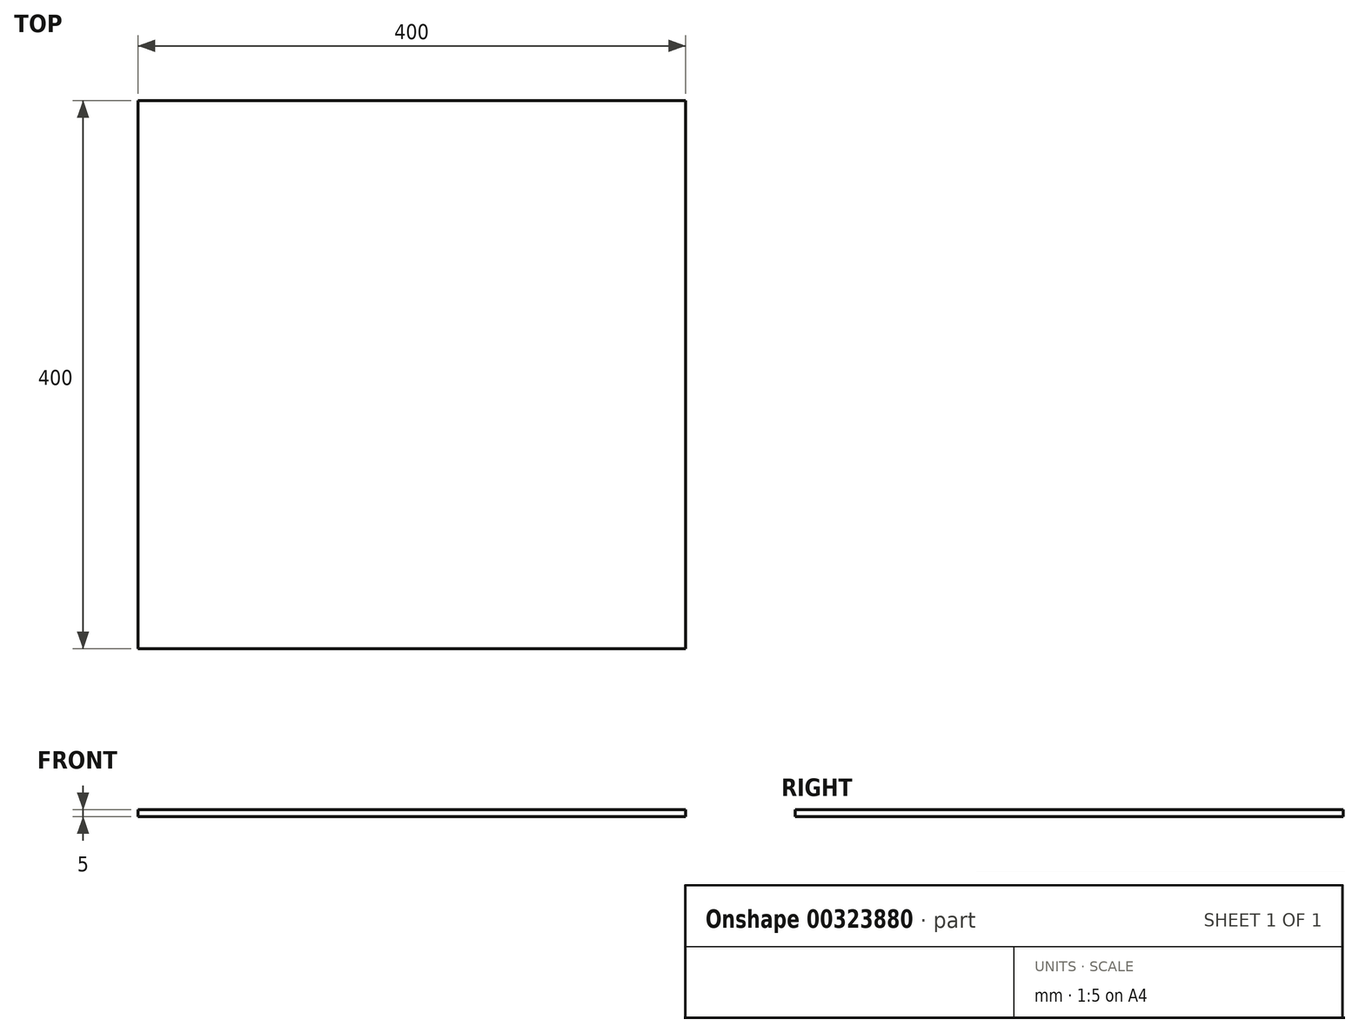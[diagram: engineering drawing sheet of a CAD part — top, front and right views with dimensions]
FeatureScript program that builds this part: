
annotation { "Feature Type Name" : "Feature", "Feature Type Description" : "" }
export const myFeature = defineFeature(function(context is Context, id is Id, definition is map)
    precondition{}
    {
        {
            var Q0;
            Q0=qCreatedBy(makeId("Top.planeOp"),FACE);
            var sketch = newSketch(context, id + "F0", { "sketchPlane" : qUnion([Q0])});
            skLineSegment(sketch, "E0.bottom", {"start": v(-200, 200) * mm, "end": v(200, 200) * mm});
            skLineSegment(sketch, "E0.top", {"start": v(-200, -200) * mm, "end": v(200, -200) * mm});
            skLineSegment(sketch, "E0.right", {"start": v(200, 200) * mm, "end": v(200, -200) * mm});
            skLineSegment(sketch, "E1", {"start": v(-200, 200) * mm, "end": v(-200, -200) * mm});
            skLineSegment(sketch, "E2", {"start": v(-200, -200) * mm, "end": v(-200, -70) * mm});
            skLineSegment(sketch, "E3", {"start": v(-200, -70) * mm, "end": v(-200, 60) * mm});
            skLineSegment(sketch, "E4", {"start": v(-200, 60) * mm, "end": v(-200, 190) * mm});
            skLineSegment(sketch, "E5", {"start": v(-200, -200) * mm, "end": v(60, -200) * mm});
            skLineSegment(sketch, "E6", {"start": v(60, -200) * mm, "end": v(60, 190) * mm});
            skLineSegment(sketch, "E7", {"start": v(60, 190) * mm, "end": v(-200, 190) * mm});
            skLineSegment(sketch, "E8", {"start": v(-200, -70) * mm, "end": v(60, -70) * mm});
            skLineSegment(sketch, "E9", {"start": v(-200, 60) * mm, "end": v(60, 60) * mm});
            skLineSegment(sketch, "E10", {"start": v(60, -200) * mm, "end": v(190, -200) * mm});
            skLineSegment(sketch, "E11", {"start": v(190, -200) * mm, "end": v(190, 60) * mm});
            skLineSegment(sketch, "E12", {"start": v(190, 60) * mm, "end": v(60, 60) * mm});
            skLineSegment(sketch, "E13", {"start": v(190, 60) * mm, "end": v(190, 180) * mm});
            skLineSegment(sketch, "E14", {"start": v(190, 180) * mm, "end": v(60, 180) * mm});
            skSolve(sketch);
        }
        {
            var Q0;
            Q0 = qSketchRegion(id + "F0", true);
            extrude(context, id + "F1", {"entities" : qUnion([Q0]), "depth" : 5 * mm});
        }
        {
            var Q0;
            {var subQ0=sQuery(id+"F0.wireOp",EDGE,"E12");Q0=makeQuery(id+"F0.imprint","IMPRINT",FACE,{"disambiguationData":[TD([[makeQuery(id+"F0.imprint","IMPRINT",EDGE,{"derivedFrom":subQ0}),-1.0]])]});}
            extrude(context, id + "F2", {"entities" : qUnion([Q0]), "operationType" : NewBodyOperationType.ADD, "depth" : 5 * mm});
        }
    });
